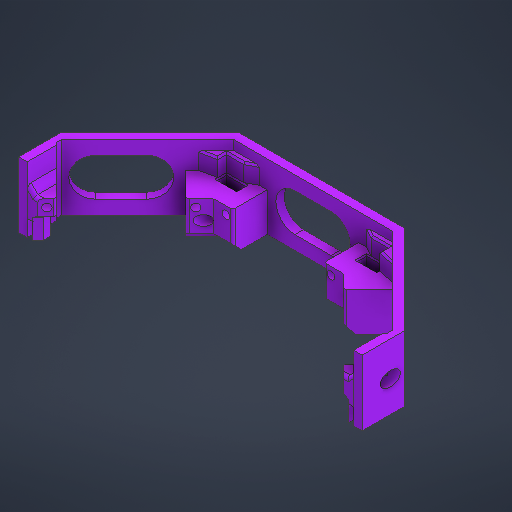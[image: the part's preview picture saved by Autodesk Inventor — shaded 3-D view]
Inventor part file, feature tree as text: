
AUTODESK INVENTOR PART (.ipt)
format: ipt  version: 2025 (Build 290162000, 162)  size: 859,648 bytes
history: native  units: mm
features: sketch x27, extrude x25, projected_geometry x11, chamfer x9, hole x6, other x2, fillet x2, mirror x1
ambient origin geometry x8: Origin, YZ Plane, XZ Plane, XY Plane, X Axis, Y Axis, Z Axis, Center Point
bodies: Body1 (feature_tree)
feature tree (83):
  other  "Těleso1"
  sketch  "Náčrt1"
  extrude  "Vysunutí1"  Depth=2.5mm
  extrude  "Vysunutí2"  Depth=23.0mm
  extrude  "Vysunutí3"  TaperAngle=135.0deg  [1 undecoded]
  extrude  "Vysunutí7"  Depth=19.0mm TaperAngle=0.0deg
  extrude  "Vysunutí9"  Depth=2.25mm
  extrude  "Vysunutí5"  Depth=9.0mm
  extrude  "Vysunutí4"  Depth=10.0mm TaperAngle=0.0deg
  sketch  "Náčrt11"
  extrude  "Vysunutí10"  Depth=15.25mm
  hole  "Díra1"  [1 undecoded]
  hole  "Díra2"  [1 undecoded]
  chamfer  "Zkosení3"  Distance=5.5mm
  sketch  "Náčrt9"
  extrude  "Vysunutí8"  Depth=10.6mm
  extrude  "Vysunutí17"  Depth=5.25mm
  extrude  "Vysunutí24"  Depth=11.5mm TaperAngle=0.0deg
  chamfer  "Zkosení4"  Distance=10.6mm
  chamfer  "Zkosení10"  Distance=10.5mm
  chamfer  "Zkosení11"  Distance=11.5mm
  extrude  "Vysunutí25"  Depth=0.2mm
  extrude  "Vysunutí21"  Depth=0.2mm
  extrude  "Vysunutí20"  Depth=49.75mm
  sketch  "Náčrt23"
  extrude  "Vysunutí22"  Depth=2.5mm
  hole  "Díra6"  [1 undecoded]
  extrude  "Vysunutí23"  TaperAngle=0.0deg  [1 undecoded]
  fillet  "Zaoblení1"  Radius=10.0mm
  extrude  "Vysunutí12"  Depth=1.0mm
  sketch  "Náčrt13"
  extrude  "Vysunutí13"  Depth=10.0mm TaperAngle=0.0deg
  extrude  "Vysunutí14"  TaperAngle=112.5deg  [1 undecoded]
  hole  "Díra3"  [1 undecoded]
  hole  "Díra4"  [1 undecoded]
  extrude  "Vysunutí30"  Depth=4.2mm
  hole  "Díra5"  [1 undecoded]
  extrude  "Vysunutí15"  Depth=4.2mm
  chamfer  "Zkosení7"  Distance=4.2mm
  chamfer  "Zkosení1"  Distance=2.0mm
  fillet  "Zaoblení3"  Radius=6.0mm
  extrude  "Vysunutí18"  Depth=2.5mm TaperAngle=45.0deg
  extrude  "Vysunutí19"  Depth=1.5mm TaperAngle=45.0deg
  chamfer  "Zkosení12"  Distance=2.0mm
  chamfer  "Zkosení13"  Distance=2.0mm
  other  "Pracovní rovina1"
  extrude  "Vysunutí29"  Depth=6.0mm
  chamfer  "Zkosení16"  Distance=4.0mm
  extrude  "Vysunutí31"  Depth=6.0mm TaperAngle=0.0deg
  mirror  "Zrcadlit1"
  sketch  "Náčrt2"
  projected_geometry  "Promítnutá smyčka1"
  sketch  "Náčrt3"
  sketch  "Náčrt4"
  projected_geometry  "Promítnutá smyčka2"
  sketch  "Náčrt5"
  sketch  "Náčrt6"
  sketch  "Náčrt7"
  sketch  "Náčrt8"
  projected_geometry  "Promítnutá smyčka4"
  projected_geometry  "Promítnutá smyčka6"
  projected_geometry  "Promítnutá smyčka7"
  sketch  "Náčrt10"
  sketch  "Náčrt12"
  sketch  "Náčrt14"
  sketch  "Náčrt15"
  sketch  "Náčrt16"
  sketch  "Náčrt17"
  projected_geometry  "Promítnutá smyčka8"
  sketch  "Náčrt19"
  sketch  "Náčrt20"
  sketch  "Náčrt22"
  projected_geometry  "Promítnutá smyčka11"
  projected_geometry  "Promítnutá smyčka12"
  sketch  "Náčrt24"
  projected_geometry  "Promítnutá smyčka14"
  sketch  "Náčrt25"
  sketch  "Náčrt26"
  projected_geometry  "Promítnutá smyčka15"
  sketch  "Náčrt31"
  sketch  "Náčrt32"
  projected_geometry  "Promítnutá smyčka19"
  sketch  "Náčrt33"
note: 9 required parameter values undecoded (feature->parameter linkage not recoverable at this tier; creation-order binding heuristic only, values carry confidence <= 0.55)
